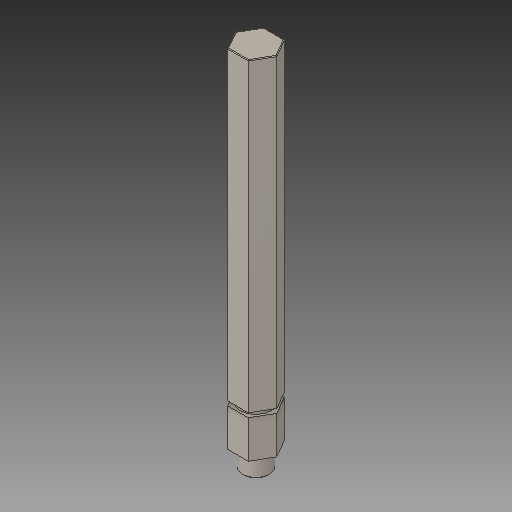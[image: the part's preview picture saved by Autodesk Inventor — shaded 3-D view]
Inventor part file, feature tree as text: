
AUTODESK INVENTOR PART (.ipt)
format: ipt  version: 2018 (Build 220112000, 112)  size: 98,304 bytes
history: native  units: in
note: dims shown in document units (in); Inventor stores cm internally (conversion verified against a paired STEP export)
features: chamfer x1
ambient origin geometry x8: Origin, YZ Plane, XZ Plane, XY Plane, X Axis, Y Axis, Z Axis, Center Point
bodies: Solid1 (feature_tree)
feature tree (1):
  chamfer  "Chamfer1"  [1 undecoded]
note: 1 required parameter value undecoded (feature->parameter linkage not recoverable at this tier; creation-order binding heuristic only, values carry confidence <= 0.55)
